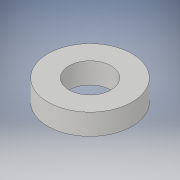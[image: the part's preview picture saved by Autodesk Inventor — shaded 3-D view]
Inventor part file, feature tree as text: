
AUTODESK INVENTOR PART (.ipt)
format: ipt  version: 2019 (Build 230136000, 136)  size: 96,768 bytes
history: native  units: in
note: dims shown in document units (in); Inventor stores cm internally (conversion verified against a paired STEP export)
features: extrude x1, sketch x1
ambient origin geometry x8: Origin, YZ Plane, XZ Plane, XY Plane, X Axis, Y Axis, Z Axis, Center Point
bodies: Solid1 (feature_tree)
feature tree (2):
  extrude  "Extrusion1"  Depth=0.5in
  sketch  "Sketch1"  dims[d0=1.0in d1=2.0in d2=0.5in d3=0.0in]
